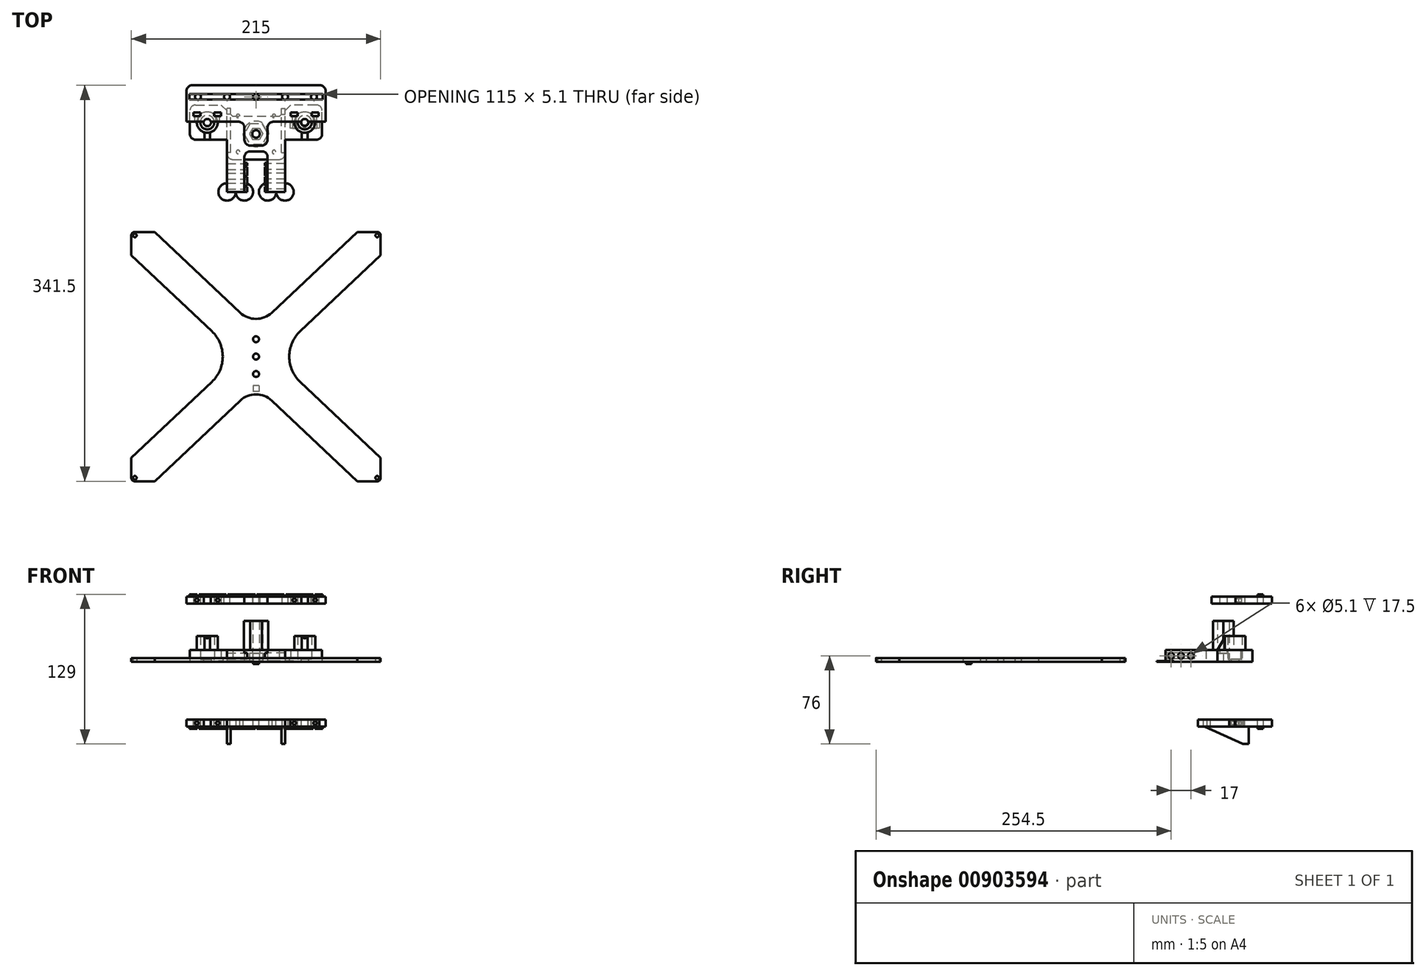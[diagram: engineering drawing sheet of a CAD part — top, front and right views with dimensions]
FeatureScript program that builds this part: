
annotation { "Feature Type Name" : "Feature", "Feature Type Description" : "" }
export const myFeature = defineFeature(function(context is Context, id is Id, definition is map)
    precondition{}
    {
        {
            var Q0;
            Q0=qCreatedBy(makeId("Top.planeOp"),FACE);
            var sketch = newSketch(context, id + "F0", { "sketchPlane" : qUnion([Q0])});
            skArc(sketch, "E0", {"start": v(0, -3.25) * mm, "mid": v(3.25, 0) * mm, "end": v(0, 3.25) * mm});
            skCircle(sketch, "E1", {"center": v(42, 10) * mm, "radius": 3.25 * mm});
            skLineSegment(sketch, "E2", {"start": v(0, -15) * mm, "end": v(5, -15) * mm});
            skLineSegment(sketch, "E3", {"start": v(10, -20) * mm, "end": v(10, -50) * mm});
            skLineSegment(sketch, "E4", {"start": v(10, -50) * mm, "end": v(25, -50) * mm});
            skLineSegment(sketch, "E5", {"start": v(25, -50) * mm, "end": v(25, -5) * mm});
            skLineSegment(sketch, "E6", {"start": v(25, -5) * mm, "end": v(52, -5) * mm});
            skLineSegment(sketch, "E7", {"start": v(57, 0) * mm, "end": v(57, 20) * mm});
            skLineSegment(sketch, "E8", {"start": v(52, 25) * mm, "end": v(30, 25) * mm});
            skLineSegment(sketch, "E9", {"start": v(30, 25) * mm, "end": v(20, 15) * mm});
            skLineSegment(sketch, "E10", {"start": v(20, 15) * mm, "end": v(0, 15) * mm});
            skPoint(sketch, "E11.visualSharp", {"position": v(10, -15) * mm});
            skArc(sketch, "E11.filletArc", {"start": v(10, -20) * mm, "mid": v(8.54, -16.46) * mm, "end": v(5, -15) * mm});
            skLineSegment(sketch, "E12", {"start": v(0, 15) * mm, "end": v(0, 3.25) * mm});
            skCircle(sketch, "E13.cCircle", {"center": v(0, 0) * mm, "radius": 5 * mm, "construction": true});
            skLineSegment(sketch, "E13.0", {"start": v(-2.89, 5) * mm, "end": v(2.89, 5) * mm, "construction": true});
            skLineSegment(sketch, "E13.1", {"start": v(2.89, 5) * mm, "end": v(5.77, 0) * mm, "construction": true});
            skLineSegment(sketch, "E13.2", {"start": v(5.77, 0) * mm, "end": v(2.89, -5) * mm, "construction": true});
            skLineSegment(sketch, "E13.3", {"start": v(2.89, -5) * mm, "end": v(-2.89, -5) * mm, "construction": true});
            skLineSegment(sketch, "E13.4", {"start": v(-2.89, -5) * mm, "end": v(-5.77, 0) * mm, "construction": true});
            skLineSegment(sketch, "E13.5", {"start": v(-5.77, 0) * mm, "end": v(-2.89, 5) * mm, "construction": true});
            skPoint(sketch, "E13.0.midPoint", {"position": v(0, 5) * mm});
            skLineSegment(sketch, "E14.trimOffspring", {"start": v(0, -3.25) * mm, "end": v(0, -15) * mm});
            skPoint(sketch, "E15.visualSharp", {"position": v(57, -5) * mm});
            skArc(sketch, "E15.filletArc", {"start": v(52, -5) * mm, "mid": v(55.54, -3.54) * mm, "end": v(57, 0) * mm});
            skPoint(sketch, "E16.visualSharp", {"position": v(57, 25) * mm});
            skArc(sketch, "E16.filletArc", {"start": v(57, 20) * mm, "mid": v(55.54, 23.54) * mm, "end": v(52, 25) * mm});
            skSolve(sketch);
        }
        {
            var Q0;
            Q0=makeQuery(id+"F0.imprint","IMPRINT",FACE,{"disambiguationData":[TD([[makeQuery(id+"F0.imprint","IMPRINT",EDGE,{"derivedFrom":sQuery(id+"F0.wireOp",EDGE,"E0")}),-1.0]])]});
            extrude(context, id + "F1", {"entities" : qUnion([Q0]), "depth" : 10 * mm});
        }
        {
            var Q0;
            Q0=makeQuery(id+"F1.opExtrude","CAP_FACE",FACE,{"disambiguationData":[OSD([sQuery(id+"F0.wireOp",EDGE,"E0"),sQuery(id+"F0.wireOp",EDGE,"E1"),sQuery(id+"F0.wireOp",EDGE,"E2"),sQuery(id+"F0.wireOp",EDGE,"E3"),sQuery(id+"F0.wireOp",EDGE,"E4"),sQuery(id+"F0.wireOp",EDGE,"E5"),sQuery(id+"F0.wireOp",EDGE,"E6"),sQuery(id+"F0.wireOp",EDGE,"E7"),sQuery(id+"F0.wireOp",EDGE,"E8"),sQuery(id+"F0.wireOp",EDGE,"E9"),sQuery(id+"F0.wireOp",EDGE,"E10"),sQuery(id+"F0.wireOp",EDGE,"E11.filletArc"),sQuery(id+"F0.wireOp",EDGE,"E12"),sQuery(id+"F0.wireOp",EDGE,"E14.trimOffspring"),sQuery(id+"F0.wireOp",EDGE,"E15.filletArc"),sQuery(id+"F0.wireOp",EDGE,"E16.filletArc")])],"isStart":false});
            var sketch = newSketch(context, id + "F2", { "sketchPlane" : qUnion([Q0])});
            skCircle(sketch, "E17", {"center": v(42, 10) * mm, "radius": 6.05 * mm});
            skCircle(sketch, "E18", {"center": v(42, 10) * mm, "radius": 9 * mm});
            skSolve(sketch);
        }
        {
            var Q0;
            Q0=qSketchRegion(id+"F2",true);
            extrude(context, id + "F3", {"entities" : qUnion([Q0]), "operationType" : NewBodyOperationType.ADD, "depth" : 12 * mm});
        }
        {
            var Q0;
            {var subQ0=sQuery(id+"F0.wireOp",EDGE,"E9");var subQ1=sQuery(id+"F0.wireOp",EDGE,"E8");var subQ2=sQuery(id+"F0.wireOp",EDGE,"E16.filletArc");var subQ3=sQuery(id+"F0.wireOp",EDGE,"E7");var subQ4=sQuery(id+"F0.wireOp",EDGE,"E15.filletArc");var subQ5=sQuery(id+"F0.wireOp",EDGE,"E6");var subQ6=sQuery(id+"F0.wireOp",EDGE,"E5");var subQ7=sQuery(id+"F0.wireOp",EDGE,"E0");var subQ8=sQuery(id+"F0.wireOp",EDGE,"E2");var subQ9=sQuery(id+"F0.wireOp",EDGE,"E10");var subQ10=sQuery(id+"F0.wireOp",EDGE,"E3");var subQ11=sQuery(id+"F0.wireOp",EDGE,"E4");var subQ12=sQuery(id+"F0.wireOp",EDGE,"E11.filletArc");var subQ13=sQuery(id+"F0.wireOp",EDGE,"E12");var subQ14=sQuery(id+"F0.wireOp",EDGE,"E14.trimOffspring");Q0=makeQuery(id+"F3.boolean.opBoolean","SPLIT",FACE,{"disambiguationData":[TD([makeQuery(id+"F1.opExtrude","SWEPT_FACE",FACE,{"disambiguationData":[OSD([subQ7])]})])],"derivedFrom":makeQuery(id+"F1.opExtrude","CAP_FACE",FACE,{"disambiguationData":[OSD([subQ7,sQuery(id+"F0.wireOp",EDGE,"E1"),subQ8,subQ10,subQ11,subQ6,subQ5,subQ3,subQ1,subQ0,subQ9,subQ12,subQ13,subQ14,subQ4,subQ2])],"isStart":false})});}
            var sketch = newSketch(context, id + "F4", { "sketchPlane" : qUnion([Q0])});
            skArc(sketch, "E19.cCircle", {"start": v(0, -5) * mm, "mid": v(4.33, -2.5) * mm, "end": v(4.33, 2.5) * mm, "construction": true});
            skLineSegment(sketch, "E19.0", {"start": v(0, 5) * mm, "end": v(2.89, 5) * mm});
            skLineSegment(sketch, "E19.1", {"start": v(2.89, 5) * mm, "end": v(5.77, 0) * mm});
            skLineSegment(sketch, "E19.2", {"start": v(5.77, 0) * mm, "end": v(2.89, -5) * mm});
            skLineSegment(sketch, "E19.3", {"start": v(2.89, -5) * mm, "end": v(0, -5) * mm});
            skPoint(sketch, "E19.0.midPoint", {"position": v(0, 5) * mm});
            skArc(sketch, "E20.cCircle", {"start": v(0, -9) * mm, "mid": v(9, 0) * mm, "end": v(0, 9) * mm, "construction": true});
            skLineSegment(sketch, "E20.0", {"start": v(0, 9) * mm, "end": v(5.2, 9) * mm});
            skLineSegment(sketch, "E20.1", {"start": v(5.2, 9) * mm, "end": v(10.4, 0) * mm});
            skLineSegment(sketch, "E20.2", {"start": v(10.4, 0) * mm, "end": v(5.2, -9) * mm});
            skLineSegment(sketch, "E20.3", {"start": v(5.2, -9) * mm, "end": v(0, -9) * mm});
            skPoint(sketch, "E20.0.midPoint", {"position": v(0, 9) * mm});
            skLineSegment(sketch, "E21", {"start": v(0, 9) * mm, "end": v(0, 5) * mm});
            skLineSegment(sketch, "E22", {"start": v(0, -9.12) * mm, "end": v(0, -5) * mm});
            skSolve(sketch);
        }
        {
            var Q0;
            Q0=qSketchRegion(id+"F4",true);
            extrude(context, id + "F5", {"entities" : qUnion([Q0]), "operationType" : NewBodyOperationType.ADD, "depth" : 25 * mm});
        }
        {
            var Q0;
            {var subQ0=sQuery(id+"F0.wireOp",EDGE,"E11.filletArc");var subQ2=sQuery(id+"F0.wireOp",EDGE,"E9");var subQ4=sQuery(id+"F0.wireOp",EDGE,"E8");var subQ6=sQuery(id+"F0.wireOp",EDGE,"E16.filletArc");var subQ8=sQuery(id+"F0.wireOp",EDGE,"E7");var subQ10=sQuery(id+"F0.wireOp",EDGE,"E15.filletArc");var subQ12=sQuery(id+"F0.wireOp",EDGE,"E6");var subQ14=sQuery(id+"F0.wireOp",EDGE,"E2");var subQ15=makeQuery(id+"F1.opExtrude","SWEPT_FACE",FACE,{"disambiguationData":[OSD([subQ14])]});var subQ16=sQuery(id+"F0.wireOp",EDGE,"E10");var subQ18=sQuery(id+"F0.wireOp",EDGE,"E3");var subQ20=sQuery(id+"F0.wireOp",EDGE,"E4");var subQ22=sQuery(id+"F0.wireOp",EDGE,"E5");var subQ24=sQuery(id+"F0.wireOp",EDGE,"E12");var subQ26=sQuery(id+"F0.wireOp",EDGE,"E14.trimOffspring");var subQ29=sQuery(id+"F0.wireOp",EDGE,"E0");Q0=makeQuery(id+"F5.boolean.opBoolean","SPLIT",FACE,{"disambiguationData":[TD([subQ15])],"derivedFrom":makeQuery(id+"F3.boolean.opBoolean","SPLIT",FACE,{"disambiguationData":[TD([makeQuery(id+"F1.opExtrude","SWEPT_FACE",FACE,{"disambiguationData":[OSD([subQ29])]})])],"derivedFrom":makeQuery(id+"F1.opExtrude","CAP_FACE",FACE,{"disambiguationData":[OSD([subQ29,sQuery(id+"F0.wireOp",EDGE,"E1"),subQ14,subQ18,subQ20,subQ22,subQ12,subQ8,subQ4,subQ2,subQ16,subQ0,subQ24,subQ26,subQ10,subQ6])],"isStart":false})})});}
            var sketch = newSketch(context, id + "F6", { "sketchPlane" : qUnion([Q0])});
            skCircle(sketch, "E23.0", {"center": v(42, 10) * mm, "radius": 6.05 * mm});
            skLineSegment(sketch, "E24.0", {"start": v(0, 5) * mm, "end": v(2.89, 5) * mm});
            skLineSegment(sketch, "E25.0", {"start": v(2.89, 5) * mm, "end": v(5.77, 0) * mm});
            skLineSegment(sketch, "E26.0", {"start": v(5.77, 0) * mm, "end": v(2.89, -5) * mm});
            skLineSegment(sketch, "E27.0", {"start": v(2.89, -5) * mm, "end": v(0, -5) * mm});
            skLineSegment(sketch, "E28", {"start": v(0, 5) * mm, "end": v(0, -5) * mm});
            skSolve(sketch);
        }
        {
            var Q0;
            Q0=makeQuery(id+"F6.imprint","IMPRINT",FACE,{"disambiguationData":[TD([[makeQuery(id+"F6.imprint","IMPRINT",EDGE,{"derivedFrom":sQuery(id+"F6.wireOp",EDGE,"E23.0")}),1.0]])]});
            extrude(context, id + "F7", {"entities" : qUnion([Q0]), "operationType" : NewBodyOperationType.REMOVE, "oppositeDirection" : true, "depth" : 8 * mm});
        }
        {
            var Q0;
            Q0=qCreatedBy(makeId("Right.planeOp"),FACE);
            cPlane(context, id + "F8", {"entities" : qUnion([Q0]), "cplaneType" : CPlaneType.OFFSET, "offset" : 42 * mm, "width" : 150 * mm, "height" : 150 * mm});
        }
        {
            var Q0;
            Q0=makeQuery(id+"F1.opExtrude","CAP_FACE",FACE,{"disambiguationData":[OSD([sQuery(id+"F0.wireOp",EDGE,"E0"),sQuery(id+"F0.wireOp",EDGE,"E1"),sQuery(id+"F0.wireOp",EDGE,"E2"),sQuery(id+"F0.wireOp",EDGE,"E3"),sQuery(id+"F0.wireOp",EDGE,"E4"),sQuery(id+"F0.wireOp",EDGE,"E5"),sQuery(id+"F0.wireOp",EDGE,"E6"),sQuery(id+"F0.wireOp",EDGE,"E7"),sQuery(id+"F0.wireOp",EDGE,"E8"),sQuery(id+"F0.wireOp",EDGE,"E9"),sQuery(id+"F0.wireOp",EDGE,"E10"),sQuery(id+"F0.wireOp",EDGE,"E11.filletArc"),sQuery(id+"F0.wireOp",EDGE,"E12"),sQuery(id+"F0.wireOp",EDGE,"E14.trimOffspring"),sQuery(id+"F0.wireOp",EDGE,"E15.filletArc"),sQuery(id+"F0.wireOp",EDGE,"E16.filletArc")])],"isStart":true});
            var sketch = newSketch(context, id + "F9", { "sketchPlane" : qUnion([Q0])});
            skLineSegment(sketch, "E29.0.0", {"start": v(0, 5) * mm, "end": v(2.89, 5) * mm});
            skLineSegment(sketch, "E29.0.1", {"start": v(2.89, 5) * mm, "end": v(5.77, 0) * mm});
            skLineSegment(sketch, "E29.0.2", {"start": v(5.77, 0) * mm, "end": v(2.89, -5) * mm});
            skLineSegment(sketch, "E29.0.3", {"start": v(2.89, -5) * mm, "end": v(0, -5) * mm});
            skLineSegment(sketch, "E29.0.4", {"start": v(0, -5) * mm, "end": v(0, -3.25) * mm});
            skArc(sketch, "E29.0.5", {"start": v(0, -3.25) * mm, "mid": v(3.25, 0) * mm, "end": v(0, 3.25) * mm});
            skLineSegment(sketch, "E29.0.6", {"start": v(0, 3.25) * mm, "end": v(0, 5) * mm});
            skSolve(sketch);
        }
        {
            var Q0;
            Q0=makeQuery(id+"F9.imprint","IMPRINT",FACE,{"disambiguationData":[TD([[makeQuery(id+"F9.imprint","IMPRINT",EDGE,{"derivedFrom":sQuery(id+"F9.wireOp",EDGE,"E29.0.0")}),-1.0]])]});
            extrude(context, id + "F10", {"entities" : qUnion([Q0]), "operationType" : NewBodyOperationType.REMOVE, "oppositeDirection" : true, "depth" : 7 * mm});
        }
        {
            var Q0;
            Q0=qCreatedBy(id+"F8.planeOp",FACE);
            var sketch = newSketch(context, id + "F11", { "sketchPlane" : qUnion([Q0])});
            skLineSegment(sketch, "E30", {"start": v(2, 22) * mm, "end": v(-4.93, 10) * mm});
            skLineSegment(sketch, "E31", {"start": v(-4.93, 10) * mm, "end": v(2, 10) * mm});
            skLineSegment(sketch, "E32", {"start": v(2, 10) * mm, "end": v(2, 22) * mm});
            skSolve(sketch);
        }
        {
            var Q0;
            Q0=makeQuery(id+"F11.imprint","IMPRINT",FACE,{"disambiguationData":[TD([[makeQuery(id+"F11.imprint","IMPRINT",EDGE,{"derivedFrom":sQuery(id+"F11.wireOp",EDGE,"E30")}),1.0]])]});
            extrude(context, id + "F12", {"entities" : qUnion([Q0]), "operationType" : NewBodyOperationType.ADD, "endBound" : BoundingType.SYMMETRIC, "depth" : 5 * mm});
        }
        {
            var Q0;
            Q0=makeQuery(id+"F1.opExtrude","SWEPT_FACE",FACE,{"disambiguationData":[OSD([sQuery(id+"F0.wireOp",EDGE,"E4")])]});
            var sketch = newSketch(context, id + "F13", { "sketchPlane" : qUnion([Q0])});
            skLineSegment(sketch, "E33.bottom", {"start": v(10, 7.5) * mm, "end": v(7.5, 7.5) * mm});
            skLineSegment(sketch, "E33.top", {"start": v(10, 2.5) * mm, "end": v(7.5, 2.5) * mm});
            skLineSegment(sketch, "E33.left", {"start": v(10, 7.5) * mm, "end": v(10, 2.5) * mm});
            skLineSegment(sketch, "E33.right", {"start": v(7.5, 7.5) * mm, "end": v(7.5, 2.5) * mm});
            skSolve(sketch);
        }
        {
            var Q0;
            Q0=qSketchRegion(id+"F13",true);
            extrude(context, id + "F14", {"entities" : qUnion([Q0]), "operationType" : NewBodyOperationType.ADD, "oppositeDirection" : true, "depth" : 25 * mm});
        }
        {
            var Q0;
            Q0=makeQuery(id+"F14.opExtrude","SWEPT_FACE",FACE,{"disambiguationData":[OSD([sQuery(id+"F13.wireOp",EDGE,"E33.right")])]});
            var sketch = newSketch(context, id + "F15", { "sketchPlane" : qUnion([Q0])});
            skCircle(sketch, "E34", {"center": v(45, 5) * mm, "radius": 2.55 * mm});
            skPoint(sketch, "E34.centerSnap0", {"position": v(50, 5) * mm});
            skCircle(sketch, "E35.1.0.0", {"center": v(36.5, 5) * mm, "radius": 2.55 * mm});
            skCircle(sketch, "E35.2.0.0", {"center": v(28, 5) * mm, "radius": 2.55 * mm});
            skLineSegment(sketch, "E35.direction1", {"start": v(45, 5) * mm, "end": v(36.5, 5) * mm, "construction": true});
            skSolve(sketch);
        }
        {
            var Q0;
            Q0=qSketchRegion(id+"F15",true);
            extrude(context, id + "F16", {"entities" : qUnion([Q0]), "operationType" : NewBodyOperationType.REMOVE, "oppositeDirection" : true, "depth" : 25 * mm});
        }
        {
            var Q0;
            Q0=makeQuery(id+"F1.opExtrude","SWEPT_BODY",BODY,{"disambiguationData":[OSD([sQuery(id+"F0.wireOp",EDGE,"E0"),sQuery(id+"F0.wireOp",EDGE,"E1"),sQuery(id+"F0.wireOp",EDGE,"E2"),sQuery(id+"F0.wireOp",EDGE,"E3"),sQuery(id+"F0.wireOp",EDGE,"E4"),sQuery(id+"F0.wireOp",EDGE,"E5"),sQuery(id+"F0.wireOp",EDGE,"E6"),sQuery(id+"F0.wireOp",EDGE,"E7"),sQuery(id+"F0.wireOp",EDGE,"E8"),sQuery(id+"F0.wireOp",EDGE,"E9"),sQuery(id+"F0.wireOp",EDGE,"E10"),sQuery(id+"F0.wireOp",EDGE,"E11.filletArc"),sQuery(id+"F0.wireOp",EDGE,"E12"),sQuery(id+"F0.wireOp",EDGE,"E14.trimOffspring"),sQuery(id+"F0.wireOp",EDGE,"E15.filletArc"),sQuery(id+"F0.wireOp",EDGE,"E16.filletArc")])]});
            var Q1;
            Q1=qCreatedBy(makeId("Right.planeOp"),FACE);
            mirror(context, id + "F17", {"operationType" : NewBodyOperationType.ADD, "entities" : qUnion([Q0]), "mirrorPlane" : qUnion([Q1])});
        }
        {
            var Q0;
            Q0=qCreatedBy(makeId("Top.planeOp"),FACE);
            cPlane(context, id + "F18", {"entities" : qUnion([Q0]), "cplaneType" : CPlaneType.OFFSET, "offset" : 50 * mm, "width" : 150 * mm, "height" : 150 * mm});
        }
        {
            var Q0;
            Q0=qCreatedBy(id+"F18.planeOp",FACE);
            var sketch = newSketch(context, id + "F19", { "sketchPlane" : qUnion([Q0])});
            skArc(sketch, "E36.0", {"start": v(-39.04, 10.5) * mm, "mid": v(-42, 13) * mm, "end": v(-44.96, 10.5) * mm});
            skCircle(sketch, "E37.0", {"center": v(0, 0) * mm, "radius": 3.25 * mm});
            skArc(sketch, "E38.0", {"start": v(44.96, 10.5) * mm, "mid": v(42, 13) * mm, "end": v(39.04, 10.5) * mm});
            skLineSegment(sketch, "E39", {"start": v(-60, 10.5) * mm, "end": v(-60, 37) * mm});
            skLineSegment(sketch, "E40", {"start": v(-55, 42) * mm, "end": v(55, 42) * mm});
            skLineSegment(sketch, "E41", {"start": v(60, 37) * mm, "end": v(60, 10.5) * mm});
            skArc(sketch, "E42.filletArc", {"start": v(-55, 42) * mm, "mid": v(-58.54, 40.54) * mm, "end": v(-60, 37) * mm});
            skPoint(sketch, "E43.visualSharp", {"position": v(60, 42) * mm});
            skArc(sketch, "E43.filletArc", {"start": v(60, 37) * mm, "mid": v(58.54, 40.54) * mm, "end": v(55, 42) * mm});
            skLineSegment(sketch, "E44", {"start": v(-10, 5.5) * mm, "end": v(-10, -5) * mm});
            skLineSegment(sketch, "E45", {"start": v(-5, -10) * mm, "end": v(5, -10) * mm});
            skLineSegment(sketch, "E46", {"start": v(10, -5) * mm, "end": v(10, 5.5) * mm});
            skLineSegment(sketch, "E47", {"start": v(15, 10.5) * mm, "end": v(39.04, 10.5) * mm});
            skLineSegment(sketch, "E48", {"start": v(-15, 10.5) * mm, "end": v(-39.04, 10.5) * mm});
            skLineSegment(sketch, "E49", {"start": v(0, 0) * mm, "end": v(0, -10) * mm, "construction": true});
            skLineSegment(sketch, "E50", {"start": v(60, 10.5) * mm, "end": v(44.96, 10.5) * mm});
            skLineSegment(sketch, "E51", {"start": v(-60, 10.5) * mm, "end": v(-44.96, 10.5) * mm});
            skLineSegment(sketch, "E52.bottom", {"start": v(-54, 18.5) * mm, "end": v(-48, 18.5) * mm});
            skLineSegment(sketch, "E52.top", {"start": v(-54, 15.5) * mm, "end": v(-48, 15.5) * mm});
            skLineSegment(sketch, "E52.left", {"start": v(-54, 18.5) * mm, "end": v(-54, 15.5) * mm});
            skLineSegment(sketch, "E52.right", {"start": v(-48, 18.5) * mm, "end": v(-48, 15.5) * mm});
            skLineSegment(sketch, "E53", {"start": v(-42, 10) * mm, "end": v(-42, 18.5) * mm, "construction": true});
            skLineSegment(sketch, "E54", {"start": v(-51, 18.5) * mm, "end": v(-51, 15.5) * mm, "construction": true});
            skLineSegment(sketch, "E55.MirrorCS", {"start": v(-36, 18.5) * mm, "end": v(-36, 15.5) * mm});
            skLineSegment(sketch, "E56.MirrorCS", {"start": v(-30, 18.5) * mm, "end": v(-36, 18.5) * mm});
            skLineSegment(sketch, "E57.MirrorCS", {"start": v(-30, 18.5) * mm, "end": v(-30, 15.5) * mm});
            skLineSegment(sketch, "E58.MirrorCS", {"start": v(-30, 15.5) * mm, "end": v(-36, 15.5) * mm});
            skLineSegment(sketch, "E59.MirrorCS", {"start": v(30, 15.5) * mm, "end": v(36, 15.5) * mm});
            skLineSegment(sketch, "E60.MirrorCS", {"start": v(30, 18.5) * mm, "end": v(36, 18.5) * mm});
            skLineSegment(sketch, "E61.MirrorCS", {"start": v(30, 18.5) * mm, "end": v(30, 15.5) * mm});
            skLineSegment(sketch, "E62.MirrorCS", {"start": v(36, 18.5) * mm, "end": v(36, 15.5) * mm});
            skLineSegment(sketch, "E63.MirrorCS", {"start": v(48, 18.5) * mm, "end": v(48, 15.5) * mm});
            skLineSegment(sketch, "E64.MirrorCS", {"start": v(54, 18.5) * mm, "end": v(48, 18.5) * mm});
            skLineSegment(sketch, "E65.MirrorCS", {"start": v(54, 18.5) * mm, "end": v(54, 15.5) * mm});
            skLineSegment(sketch, "E66.MirrorCS", {"start": v(54, 15.5) * mm, "end": v(48, 15.5) * mm});
            skPoint(sketch, "E67.visualSharp", {"position": v(-10, 10.5) * mm});
            skArc(sketch, "E67.filletArc", {"start": v(-10, 5.5) * mm, "mid": v(-11.46, 9.04) * mm, "end": v(-15, 10.5) * mm});
            skPoint(sketch, "E68.visualSharp", {"position": v(10, 10.5) * mm});
            skArc(sketch, "E68.filletArc", {"start": v(15, 10.5) * mm, "mid": v(11.46, 9.04) * mm, "end": v(10, 5.5) * mm});
            skPoint(sketch, "E69.visualSharp", {"position": v(10, -10) * mm});
            skArc(sketch, "E69.filletArc", {"start": v(5, -10) * mm, "mid": v(8.54, -8.54) * mm, "end": v(10, -5) * mm});
            skPoint(sketch, "E70.visualSharp", {"position": v(-10, -10) * mm});
            skArc(sketch, "E70.filletArc", {"start": v(-10, -5) * mm, "mid": v(-8.54, -8.54) * mm, "end": v(-5, -10) * mm});
            skSolve(sketch);
        }
        {
            var Q0;
            Q0=makeQuery(id+"F19.imprint","IMPRINT",FACE,{"disambiguationData":[TD([[makeQuery(id+"F19.imprint","IMPRINT",EDGE,{"derivedFrom":sQuery(id+"F19.wireOp",EDGE,"E36.0")}),-1.0]])]});
            extrude(context, id + "F20", {"entities" : qUnion([Q0]), "depth" : 6 * mm});
        }
        {
            var Q0;
            Q0=makeQuery(id+"F20.opExtrude","SWEPT_FACE",FACE,{"disambiguationData":[OSD([sQuery(id+"F19.wireOp",EDGE,"E52.top")])]});
            var sketch = newSketch(context, id + "F21", { "sketchPlane" : qUnion([Q0])});
            skCircle(sketch, "E71", {"center": v(51, 53) * mm, "radius": 1.55 * mm});
            skPoint(sketch, "E71.centerSnap0", {"position": v(51, 56) * mm});
            skLineSegment(sketch, "E72", {"start": v(54, 53) * mm, "end": v(51, 53) * mm, "construction": true});
            skCircle(sketch, "E73", {"center": v(33, 53) * mm, "radius": 1.55 * mm});
            skLineSegment(sketch, "E74", {"start": v(0, 59.79) * mm, "end": v(0, 45.57) * mm, "construction": true});
            skCircle(sketch, "E75.MirrorC", {"center": v(-33, 53) * mm, "radius": 1.55 * mm});
            skCircle(sketch, "E76.MirrorC", {"center": v(-51, 53) * mm, "radius": 1.55 * mm});
            skSolve(sketch);
        }
        {
            var Q0;
            Q0=qSketchRegion(id+"F21",true);
            extrude(context, id + "F22", {"entities" : qUnion([Q0]), "operationType" : NewBodyOperationType.REMOVE, "oppositeDirection" : true, "depth" : 10 * mm});
        }
        {
            var Q0;
            Q0=qCreatedBy(makeId("Right.planeOp"),FACE);
            var sketch = newSketch(context, id + "F23", { "sketchPlane" : qUnion([Q0])});
            skLineSegment(sketch, "E77", {"start": v(29.55, 56) * mm, "end": v(29.55, 58) * mm});
            skLineSegment(sketch, "E78", {"start": v(29.55, 58) * mm, "end": v(34.45, 58) * mm});
            skLineSegment(sketch, "E79", {"start": v(34.45, 58) * mm, "end": v(34.45, 56) * mm});
            skPoint(sketch, "E80", {"position": v(32, 58) * mm});
            skLineSegment(sketch, "E81", {"start": v(29.55, 56) * mm, "end": v(34.45, 56) * mm});
            skSolve(sketch);
        }
        {
            var Q0;
            Q0=makeQuery(id+"F23.imprint","IMPRINT",FACE,{"disambiguationData":[TD([[makeQuery(id+"F23.imprint","IMPRINT",EDGE,{"derivedFrom":sQuery(id+"F23.wireOp",EDGE,"E77")}),-1.0]])]});
            extrude(context, id + "F24", {"entities" : qUnion([Q0]), "operationType" : NewBodyOperationType.ADD, "endBound" : BoundingType.SYMMETRIC, "depth" : 115 * mm});
        }
        {
            var Q0;
            Q0=makeQuery(id+"F24.opExtrude","SWEPT_FACE",FACE,{"disambiguationData":[OSD([sQuery(id+"F23.wireOp",EDGE,"E78")])]});
            var sketch = newSketch(context, id + "F25", { "sketchPlane" : qUnion([Q0])});
            skCircle(sketch, "E82", {"center": v(0, 32) * mm, "radius": 2.55 * mm});
            skCircle(sketch, "E83", {"center": v(25, 32) * mm, "radius": 2.55 * mm});
            skCircle(sketch, "E84", {"center": v(50, 32) * mm, "radius": 2.55 * mm});
            skCircle(sketch, "E85", {"center": v(-25, 32) * mm, "radius": 2.55 * mm});
            skCircle(sketch, "E86", {"center": v(-50, 32) * mm, "radius": 2.55 * mm});
            skLineSegment(sketch, "E87", {"start": v(-50, 32) * mm, "end": v(-25, 32) * mm, "construction": true});
            skLineSegment(sketch, "E88", {"start": v(-25, 32) * mm, "end": v(0, 32) * mm, "construction": true});
            skLineSegment(sketch, "E89", {"start": v(25, 32) * mm, "end": v(0, 32) * mm, "construction": true});
            skLineSegment(sketch, "E90", {"start": v(50, 32) * mm, "end": v(25, 32) * mm, "construction": true});
            skSolve(sketch);
        }
        {
            var Q0;
            Q0=qSketchRegion(id+"F25",true);
            extrude(context, id + "F26", {"entities" : qUnion([Q0]), "operationType" : NewBodyOperationType.REMOVE, "oppositeDirection" : true, "depth" : 10 * mm});
        }
        {
            var Q0;
            Q0=qCreatedBy(makeId("Top.planeOp"),FACE);
            cPlane(context, id + "F27", {"entities" : qUnion([Q0]), "cplaneType" : CPlaneType.OFFSET, "offset" : 50 * mm, "oppositeDirection" : true, "width" : 150 * mm, "height" : 150 * mm});
        }
        {
            var Q0;
            Q0=qCreatedBy(id+"F27.planeOp",FACE);
            var sketch = newSketch(context, id + "F28", { "sketchPlane" : qUnion([Q0])});
            skArc(sketch, "E91.0", {"start": v(-39.04, 10.5) * mm, "mid": v(-42, 13) * mm, "end": v(-44.96, 10.5) * mm});
            skLineSegment(sketch, "E92.0", {"start": v(-60, 10.5) * mm, "end": v(-44.96, 10.5) * mm});
            skArc(sketch, "E93.0", {"start": v(44.96, 10.5) * mm, "mid": v(42, 13) * mm, "end": v(39.04, 10.5) * mm});
            skLineSegment(sketch, "E94.0", {"start": v(60, 10.5) * mm, "end": v(44.96, 10.5) * mm});
            skLineSegment(sketch, "E95.0", {"start": v(60, 37) * mm, "end": v(60, 10.5) * mm});
            skArc(sketch, "E96.0", {"start": v(60, 37) * mm, "mid": v(58.54, 40.54) * mm, "end": v(55, 42) * mm});
            skLineSegment(sketch, "E97.0", {"start": v(-55, 42) * mm, "end": v(55, 42) * mm});
            skArc(sketch, "E98.0", {"start": v(-55, 42) * mm, "mid": v(-58.54, 40.54) * mm, "end": v(-60, 37) * mm});
            skLineSegment(sketch, "E99.0", {"start": v(-60, 10.5) * mm, "end": v(-60, 37) * mm});
            skLineSegment(sketch, "E100.0", {"start": v(-54, 18.5) * mm, "end": v(-48, 18.5) * mm});
            skLineSegment(sketch, "E101.0", {"start": v(-48, 18.5) * mm, "end": v(-48, 15.5) * mm});
            skLineSegment(sketch, "E102.0", {"start": v(-54, 15.5) * mm, "end": v(-48, 15.5) * mm});
            skLineSegment(sketch, "E103.0", {"start": v(-54, 18.5) * mm, "end": v(-54, 15.5) * mm});
            skLineSegment(sketch, "E104.0", {"start": v(-30, 18.5) * mm, "end": v(-36, 18.5) * mm});
            skLineSegment(sketch, "E105.0", {"start": v(-36, 18.5) * mm, "end": v(-36, 15.5) * mm});
            skLineSegment(sketch, "E106.0", {"start": v(-30, 15.5) * mm, "end": v(-36, 15.5) * mm});
            skLineSegment(sketch, "E107.0", {"start": v(-30, 18.5) * mm, "end": v(-30, 15.5) * mm});
            skLineSegment(sketch, "E108.0", {"start": v(30, 18.5) * mm, "end": v(30, 15.5) * mm});
            skLineSegment(sketch, "E109.0", {"start": v(30, 18.5) * mm, "end": v(36, 18.5) * mm});
            skLineSegment(sketch, "E110.0", {"start": v(36, 18.5) * mm, "end": v(36, 15.5) * mm});
            skLineSegment(sketch, "E111.0", {"start": v(30, 15.5) * mm, "end": v(36, 15.5) * mm});
            skLineSegment(sketch, "E112.0", {"start": v(48, 18.5) * mm, "end": v(48, 15.5) * mm});
            skLineSegment(sketch, "E113.0", {"start": v(54, 18.5) * mm, "end": v(48, 18.5) * mm});
            skLineSegment(sketch, "E114.0", {"start": v(54, 18.5) * mm, "end": v(54, 15.5) * mm});
            skLineSegment(sketch, "E115.0", {"start": v(54, 15.5) * mm, "end": v(48, 15.5) * mm});
            skCircle(sketch, "E116", {"center": v(0, 0) * mm, "radius": 11 * mm});
            skLineSegment(sketch, "E117.bottom", {"start": v(-15.5, -15.5) * mm, "end": v(15.5, -15.5) * mm, "construction": true});
            skLineSegment(sketch, "E117.top", {"start": v(-15.5, 15.5) * mm, "end": v(15.5, 15.5) * mm, "construction": true});
            skLineSegment(sketch, "E117.left", {"start": v(-15.5, -15.5) * mm, "end": v(-15.5, 15.5) * mm, "construction": true});
            skLineSegment(sketch, "E117.right", {"start": v(15.5, -15.5) * mm, "end": v(15.5, 15.5) * mm, "construction": true});
            skCircle(sketch, "E118", {"center": v(-15.5, -15.5) * mm, "radius": 1.55 * mm});
            skCircle(sketch, "E119", {"center": v(15.5, -15.5) * mm, "radius": 1.55 * mm});
            skCircle(sketch, "E120", {"center": v(15.5, 15.5) * mm, "radius": 1.55 * mm});
            skCircle(sketch, "E121", {"center": v(-15.5, 15.5) * mm, "radius": 1.55 * mm});
            skLineSegment(sketch, "E122", {"start": v(-20, -22) * mm, "end": v(20, -22) * mm});
            skPoint(sketch, "E123", {"position": v(0, -22) * mm});
            skLineSegment(sketch, "E124", {"start": v(-25, -17) * mm, "end": v(-25, 8) * mm});
            skLineSegment(sketch, "E125", {"start": v(25, -17) * mm, "end": v(25, 8) * mm});
            skLineSegment(sketch, "E126.trimOffspring", {"start": v(-27.5, 10.5) * mm, "end": v(-39.04, 10.5) * mm});
            skLineSegment(sketch, "E127.trimOffspring", {"start": v(27.5, 10.5) * mm, "end": v(39.04, 10.5) * mm});
            skPoint(sketch, "E128.visualSharp", {"position": v(-25, -22) * mm});
            skArc(sketch, "E128.filletArc", {"start": v(-25, -17) * mm, "mid": v(-23.54, -20.54) * mm, "end": v(-20, -22) * mm});
            skPoint(sketch, "E129.visualSharp", {"position": v(-25, 10.5) * mm});
            skArc(sketch, "E129.filletArc", {"start": v(-25, 8) * mm, "mid": v(-25.73, 9.77) * mm, "end": v(-27.5, 10.5) * mm});
            skPoint(sketch, "E130.visualSharp", {"position": v(25, -22) * mm});
            skArc(sketch, "E130.filletArc", {"start": v(20, -22) * mm, "mid": v(23.54, -20.54) * mm, "end": v(25, -17) * mm});
            skPoint(sketch, "E131.visualSharp", {"position": v(25, 10.5) * mm});
            skArc(sketch, "E131.filletArc", {"start": v(27.5, 10.5) * mm, "mid": v(25.73, 9.77) * mm, "end": v(25, 8) * mm});
            skSolve(sketch);
        }
        {
            var Q0;
            Q0=makeQuery(id+"F28.imprint","IMPRINT",FACE,{"disambiguationData":[TD([[makeQuery(id+"F28.imprint","IMPRINT",EDGE,{"derivedFrom":sQuery(id+"F28.wireOp",EDGE,"E91.0")}),-1.0]])]});
            extrude(context, id + "F29", {"entities" : qUnion([Q0]), "oppositeDirection" : true, "depth" : 6 * mm});
        }
        {
            var Q0;
            Q0=makeQuery(id+"F29.opExtrude","SWEPT_FACE",FACE,{"disambiguationData":[OSD([sQuery(id+"F28.wireOp",EDGE,"E102.0")])]});
            var sketch = newSketch(context, id + "F30", { "sketchPlane" : qUnion([Q0])});
            skCircle(sketch, "E132", {"center": v(51, -53) * mm, "radius": 1.55 * mm});
            skPoint(sketch, "E132.centerSnap0", {"position": v(54, -53) * mm});
            skPoint(sketch, "E132.centerSnap1", {"position": v(51, -50) * mm});
            skCircle(sketch, "E133", {"center": v(33, -53) * mm, "radius": 1.55 * mm});
            skLineSegment(sketch, "E134", {"start": v(0, -41.03) * mm, "end": v(0, -69.82) * mm, "construction": true});
            skCircle(sketch, "E135.MirrorC", {"center": v(-33, -53) * mm, "radius": 1.55 * mm});
            skCircle(sketch, "E136.MirrorC", {"center": v(-51, -53) * mm, "radius": 1.55 * mm});
            skSolve(sketch);
        }
        {
            var Q0;
            Q0=qSketchRegion(id+"F30",true);
            extrude(context, id + "F31", {"entities" : qUnion([Q0]), "operationType" : NewBodyOperationType.REMOVE, "oppositeDirection" : true, "depth" : 10 * mm});
        }
        {
            var Q0;
            Q0=qCreatedBy(makeId("Right.planeOp"),FACE);
            var sketch = newSketch(context, id + "F32", { "sketchPlane" : qUnion([Q0])});
            skLineSegment(sketch, "E137", {"start": v(34.45, -56) * mm, "end": v(34.45, -58) * mm});
            skLineSegment(sketch, "E138", {"start": v(34.45, -58) * mm, "end": v(29.55, -58) * mm});
            skLineSegment(sketch, "E139", {"start": v(29.55, -58) * mm, "end": v(29.55, -56) * mm});
            skLineSegment(sketch, "E140", {"start": v(29.55, -56) * mm, "end": v(34.45, -56) * mm});
            skPoint(sketch, "E141", {"position": v(32, -58) * mm});
            skSolve(sketch);
        }
        {
            var Q0;
            Q0=makeQuery(id+"F32.imprint","IMPRINT",FACE,{"disambiguationData":[TD([[makeQuery(id+"F32.imprint","IMPRINT",EDGE,{"derivedFrom":sQuery(id+"F32.wireOp",EDGE,"E137")}),-1.0]])]});
            extrude(context, id + "F33", {"entities" : qUnion([Q0]), "operationType" : NewBodyOperationType.ADD, "endBound" : BoundingType.SYMMETRIC, "depth" : 115 * mm});
        }
        {
            var Q0;
            Q0=makeQuery(id+"F29.opExtrude","CAP_FACE",FACE,{"disambiguationData":[OSD([sQuery(id+"F28.wireOp",EDGE,"E91.0"),sQuery(id+"F28.wireOp",EDGE,"E92.0"),sQuery(id+"F28.wireOp",EDGE,"E93.0"),sQuery(id+"F28.wireOp",EDGE,"E94.0"),sQuery(id+"F28.wireOp",EDGE,"E95.0"),sQuery(id+"F28.wireOp",EDGE,"E96.0"),sQuery(id+"F28.wireOp",EDGE,"E97.0"),sQuery(id+"F28.wireOp",EDGE,"E98.0"),sQuery(id+"F28.wireOp",EDGE,"E99.0"),sQuery(id+"F28.wireOp",EDGE,"E100.0"),sQuery(id+"F28.wireOp",EDGE,"E101.0"),sQuery(id+"F28.wireOp",EDGE,"E102.0"),sQuery(id+"F28.wireOp",EDGE,"E103.0"),sQuery(id+"F28.wireOp",EDGE,"E104.0"),sQuery(id+"F28.wireOp",EDGE,"E105.0"),sQuery(id+"F28.wireOp",EDGE,"E106.0"),sQuery(id+"F28.wireOp",EDGE,"E107.0"),sQuery(id+"F28.wireOp",EDGE,"E108.0"),sQuery(id+"F28.wireOp",EDGE,"E109.0"),sQuery(id+"F28.wireOp",EDGE,"E110.0"),sQuery(id+"F28.wireOp",EDGE,"E111.0"),sQuery(id+"F28.wireOp",EDGE,"E112.0"),sQuery(id+"F28.wireOp",EDGE,"E113.0"),sQuery(id+"F28.wireOp",EDGE,"E114.0"),sQuery(id+"F28.wireOp",EDGE,"E115.0"),sQuery(id+"F28.wireOp",EDGE,"E116"),sQuery(id+"F28.wireOp",EDGE,"E118"),sQuery(id+"F28.wireOp",EDGE,"E119"),sQuery(id+"F28.wireOp",EDGE,"E120"),sQuery(id+"F28.wireOp",EDGE,"E121"),sQuery(id+"F28.wireOp",EDGE,"E122"),sQuery(id+"F28.wireOp",EDGE,"E124"),sQuery(id+"F28.wireOp",EDGE,"E125"),sQuery(id+"F28.wireOp",EDGE,"E126.trimOffspring"),sQuery(id+"F28.wireOp",EDGE,"E127.trimOffspring"),sQuery(id+"F28.wireOp",EDGE,"E128.filletArc"),sQuery(id+"F28.wireOp",EDGE,"E129.filletArc"),sQuery(id+"F28.wireOp",EDGE,"E130.filletArc"),sQuery(id+"F28.wireOp",EDGE,"E131.filletArc")])],"isStart":true});
            var sketch = newSketch(context, id + "F34", { "sketchPlane" : qUnion([Q0])});
            skCircle(sketch, "E142.0", {"center": v(-50, 32) * mm, "radius": 2.55 * mm});
            skCircle(sketch, "E143.0", {"center": v(-25, 32) * mm, "radius": 2.55 * mm});
            skCircle(sketch, "E144.0", {"center": v(0, 32) * mm, "radius": 2.55 * mm});
            skCircle(sketch, "E145.0", {"center": v(25, 32) * mm, "radius": 2.55 * mm});
            skCircle(sketch, "E146.0", {"center": v(50, 32) * mm, "radius": 2.55 * mm});
            skSolve(sketch);
        }
        {
            var Q0;
            Q0=qSketchRegion(id+"F34",true);
            extrude(context, id + "F35", {"entities" : qUnion([Q0]), "operationType" : NewBodyOperationType.REMOVE, "oppositeDirection" : true, "depth" : 10 * mm});
        }
        {
            var Q0;
            Q0=makeQuery(id+"F29.opExtrude","SWEPT_FACE",FACE,{"disambiguationData":[OSD([sQuery(id+"F28.wireOp",EDGE,"E125")])]});
            var sketch = newSketch(context, id + "F36", { "sketchPlane" : qUnion([Q0])});
            skLineSegment(sketch, "E147", {"start": v(-16.1, -56) * mm, "end": v(16.9, -71) * mm});
            skLineSegment(sketch, "E148", {"start": v(16.9, -71) * mm, "end": v(21.9, -71) * mm});
            skLineSegment(sketch, "E149", {"start": v(21.9, -71) * mm, "end": v(21.9, -56) * mm});
            skLineSegment(sketch, "E150", {"start": v(-16.1, -56) * mm, "end": v(21.9, -56) * mm});
            skSolve(sketch);
        }
        {
            var Q0;
            Q0=qSketchRegion(id+"F36",true);
            extrude(context, id + "F37", {"entities" : qUnion([Q0]), "operationType" : NewBodyOperationType.ADD, "oppositeDirection" : true, "depth" : 3 * mm});
        }
        {
            var Q0;
            Q0=makeQuery(id+"F29.opExtrude","SWEPT_BODY",BODY,{"disambiguationData":[OSD([sQuery(id+"F28.wireOp",EDGE,"E91.0"),sQuery(id+"F28.wireOp",EDGE,"E92.0"),sQuery(id+"F28.wireOp",EDGE,"E93.0"),sQuery(id+"F28.wireOp",EDGE,"E94.0"),sQuery(id+"F28.wireOp",EDGE,"E95.0"),sQuery(id+"F28.wireOp",EDGE,"E96.0"),sQuery(id+"F28.wireOp",EDGE,"E97.0"),sQuery(id+"F28.wireOp",EDGE,"E98.0"),sQuery(id+"F28.wireOp",EDGE,"E99.0"),sQuery(id+"F28.wireOp",EDGE,"E100.0"),sQuery(id+"F28.wireOp",EDGE,"E101.0"),sQuery(id+"F28.wireOp",EDGE,"E102.0"),sQuery(id+"F28.wireOp",EDGE,"E103.0"),sQuery(id+"F28.wireOp",EDGE,"E104.0"),sQuery(id+"F28.wireOp",EDGE,"E105.0"),sQuery(id+"F28.wireOp",EDGE,"E106.0"),sQuery(id+"F28.wireOp",EDGE,"E107.0"),sQuery(id+"F28.wireOp",EDGE,"E108.0"),sQuery(id+"F28.wireOp",EDGE,"E109.0"),sQuery(id+"F28.wireOp",EDGE,"E110.0"),sQuery(id+"F28.wireOp",EDGE,"E111.0"),sQuery(id+"F28.wireOp",EDGE,"E112.0"),sQuery(id+"F28.wireOp",EDGE,"E113.0"),sQuery(id+"F28.wireOp",EDGE,"E114.0"),sQuery(id+"F28.wireOp",EDGE,"E115.0"),sQuery(id+"F28.wireOp",EDGE,"E116"),sQuery(id+"F28.wireOp",EDGE,"E118"),sQuery(id+"F28.wireOp",EDGE,"E119"),sQuery(id+"F28.wireOp",EDGE,"E120"),sQuery(id+"F28.wireOp",EDGE,"E121"),sQuery(id+"F28.wireOp",EDGE,"E122"),sQuery(id+"F28.wireOp",EDGE,"E124"),sQuery(id+"F28.wireOp",EDGE,"E125"),sQuery(id+"F28.wireOp",EDGE,"E126.trimOffspring"),sQuery(id+"F28.wireOp",EDGE,"E127.trimOffspring"),sQuery(id+"F28.wireOp",EDGE,"E128.filletArc"),sQuery(id+"F28.wireOp",EDGE,"E129.filletArc"),sQuery(id+"F28.wireOp",EDGE,"E130.filletArc"),sQuery(id+"F28.wireOp",EDGE,"E131.filletArc")])]});
            var Q1;
            Q1=qCreatedBy(makeId("Right.planeOp"),FACE);
            mirror(context, id + "F38", {"operationType" : NewBodyOperationType.ADD, "entities" : qUnion([Q0]), "mirrorPlane" : qUnion([Q1])});
        }
        {
            var Q0;
            Q0=makeQuery(id+"F29.opExtrude","CAP_FACE",FACE,{"disambiguationData":[OSD([sQuery(id+"F28.wireOp",EDGE,"E91.0"),sQuery(id+"F28.wireOp",EDGE,"E92.0"),sQuery(id+"F28.wireOp",EDGE,"E93.0"),sQuery(id+"F28.wireOp",EDGE,"E94.0"),sQuery(id+"F28.wireOp",EDGE,"E95.0"),sQuery(id+"F28.wireOp",EDGE,"E96.0"),sQuery(id+"F28.wireOp",EDGE,"E97.0"),sQuery(id+"F28.wireOp",EDGE,"E98.0"),sQuery(id+"F28.wireOp",EDGE,"E99.0"),sQuery(id+"F28.wireOp",EDGE,"E100.0"),sQuery(id+"F28.wireOp",EDGE,"E101.0"),sQuery(id+"F28.wireOp",EDGE,"E102.0"),sQuery(id+"F28.wireOp",EDGE,"E103.0"),sQuery(id+"F28.wireOp",EDGE,"E104.0"),sQuery(id+"F28.wireOp",EDGE,"E105.0"),sQuery(id+"F28.wireOp",EDGE,"E106.0"),sQuery(id+"F28.wireOp",EDGE,"E107.0"),sQuery(id+"F28.wireOp",EDGE,"E108.0"),sQuery(id+"F28.wireOp",EDGE,"E109.0"),sQuery(id+"F28.wireOp",EDGE,"E110.0"),sQuery(id+"F28.wireOp",EDGE,"E111.0"),sQuery(id+"F28.wireOp",EDGE,"E112.0"),sQuery(id+"F28.wireOp",EDGE,"E113.0"),sQuery(id+"F28.wireOp",EDGE,"E114.0"),sQuery(id+"F28.wireOp",EDGE,"E115.0"),sQuery(id+"F28.wireOp",EDGE,"E116"),sQuery(id+"F28.wireOp",EDGE,"E118"),sQuery(id+"F28.wireOp",EDGE,"E119"),sQuery(id+"F28.wireOp",EDGE,"E120"),sQuery(id+"F28.wireOp",EDGE,"E121"),sQuery(id+"F28.wireOp",EDGE,"E122"),sQuery(id+"F28.wireOp",EDGE,"E124"),sQuery(id+"F28.wireOp",EDGE,"E125"),sQuery(id+"F28.wireOp",EDGE,"E126.trimOffspring"),sQuery(id+"F28.wireOp",EDGE,"E127.trimOffspring"),sQuery(id+"F28.wireOp",EDGE,"E128.filletArc"),sQuery(id+"F28.wireOp",EDGE,"E129.filletArc"),sQuery(id+"F28.wireOp",EDGE,"E130.filletArc"),sQuery(id+"F28.wireOp",EDGE,"E131.filletArc")])],"isStart":true});
            var sketch = newSketch(context, id + "F39", { "sketchPlane" : qUnion([Q0])});
            skArc(sketch, "E151", {"start": v(39, 10) * mm, "mid": v(42, 7) * mm, "end": v(45, 10) * mm});
            skLineSegment(sketch, "E152", {"start": v(45, 10) * mm, "end": v(54.5, 10) * mm});
            skLineSegment(sketch, "E153", {"start": v(54.5, 10) * mm, "end": v(54.5, 5) * mm});
            skLineSegment(sketch, "E154", {"start": v(54.5, 5) * mm, "end": v(29.5, 5) * mm});
            skLineSegment(sketch, "E155", {"start": v(29.5, 5) * mm, "end": v(29.5, 10) * mm});
            skLineSegment(sketch, "E156", {"start": v(29.5, 10) * mm, "end": v(39, 10) * mm});
            skSolve(sketch);
        }
        {
            var Q0;
            Q0=qSketchRegion(id+"F39",true);
            extrude(context, id + "F40", {"entities" : qUnion([Q0]), "oppositeDirection" : true, "depth" : 6 * mm});
        }
        {
            var Q0;
            Q0=makeQuery(id+"F40.opExtrude","SWEPT_FACE",FACE,{"disambiguationData":[OSD([sQuery(id+"F39.wireOp",EDGE,"E154")])]});
            var sketch = newSketch(context, id + "F41", { "sketchPlane" : qUnion([Q0])});
            skCircle(sketch, "E157.0", {"center": v(33, -53) * mm, "radius": 1.55 * mm});
            skCircle(sketch, "E158.0", {"center": v(51, -53) * mm, "radius": 1.55 * mm});
            skSolve(sketch);
        }
        {
            var Q0;
            Q0=qSketchRegion(id+"F41",true);
            extrude(context, id + "F42", {"entities" : qUnion([Q0]), "operationType" : NewBodyOperationType.REMOVE, "oppositeDirection" : true, "depth" : 6 * mm});
        }
        {
            var Q0;
            Q0=qCreatedBy(makeId("Top.planeOp"),FACE);
            var sketch = newSketch(context, id + "F43", { "sketchPlane" : qUnion([Q0])});
            skLineSegment(sketch, "E159.bottom", {"start": v(104.5, -87.5) * mm, "end": v(-104.5, -87.5) * mm, "construction": true});
            skLineSegment(sketch, "E159.top", {"start": v(104.5, -296.5) * mm, "end": v(-104.5, -296.5) * mm, "construction": true});
            skLineSegment(sketch, "E159.left", {"start": v(104.5, -87.5) * mm, "end": v(104.5, -296.5) * mm, "construction": true});
            skLineSegment(sketch, "E159.right", {"start": v(-104.5, -87.5) * mm, "end": v(-104.5, -296.5) * mm, "construction": true});
            skPoint(sketch, "E159.middle", {"position": v(0, -192) * mm});
            skCircle(sketch, "E160", {"center": v(-104.5, -87.5) * mm, "radius": 1.55 * mm});
            skCircle(sketch, "E161", {"center": v(104.5, -87.5) * mm, "radius": 1.55 * mm});
            skCircle(sketch, "E162", {"center": v(104.5, -296.5) * mm, "radius": 1.55 * mm});
            skCircle(sketch, "E163", {"center": v(-104.5, -296.5) * mm, "radius": 1.55 * mm});
            skLineSegment(sketch, "E164.bottom", {"start": v(15, -167) * mm, "end": v(-15, -167) * mm, "construction": true});
            skLineSegment(sketch, "E164.top", {"start": v(15, -217) * mm, "end": v(-15, -217) * mm, "construction": true});
            skLineSegment(sketch, "E164.left", {"start": v(15, -167) * mm, "end": v(15, -217) * mm, "construction": true});
            skLineSegment(sketch, "E164.right", {"start": v(-15, -167) * mm, "end": v(-15, -217) * mm, "construction": true});
            skLineSegment(sketch, "E165", {"start": v(87.36, -84.5) * mm, "end": v(104.5, -84.5) * mm});
            skLineSegment(sketch, "E166", {"start": v(107.5, -87.5) * mm, "end": v(107.5, -104.65) * mm});
            skPoint(sketch, "E167.visualSharp", {"position": v(107.5, -84.5) * mm});
            skArc(sketch, "E167.filletArc", {"start": v(107.5, -87.5) * mm, "mid": v(106.62, -85.38) * mm, "end": v(104.5, -84.5) * mm});
            skLineSegment(sketch, "E168", {"start": v(87.36, -84.5) * mm, "end": v(13.73, -154.03) * mm});
            skLineSegment(sketch, "E169", {"start": v(107.5, -104.65) * mm, "end": v(38.1, -170.2) * mm});
            skLineSegment(sketch, "E170", {"start": v(87.36, -299.5) * mm, "end": v(104.5, -299.5) * mm});
            skLineSegment(sketch, "E171", {"start": v(107.5, -296.5) * mm, "end": v(107.5, -279.36) * mm});
            skPoint(sketch, "E172.visualSharp", {"position": v(107.5, -299.5) * mm});
            skArc(sketch, "E172.filletArc", {"start": v(104.5, -299.5) * mm, "mid": v(106.62, -298.62) * mm, "end": v(107.5, -296.5) * mm});
            skLineSegment(sketch, "E173", {"start": v(107.5, -279.36) * mm, "end": v(38.1, -213.81) * mm});
            skLineSegment(sketch, "E174", {"start": v(87.36, -299.5) * mm, "end": v(13.73, -229.97) * mm});
            skLineSegment(sketch, "E175", {"start": v(0, -192) * mm, "end": v(0, -167) * mm, "construction": true});
            skLineSegment(sketch, "E176.MirrorCS", {"start": v(-87.36, -84.5) * mm, "end": v(-13.73, -154.03) * mm});
            skLineSegment(sketch, "E177.MirrorCS", {"start": v(-107.5, -104.65) * mm, "end": v(-38.1, -170.2) * mm});
            skLineSegment(sketch, "E178.MirrorCS", {"start": v(-107.5, -279.36) * mm, "end": v(-38.1, -213.81) * mm});
            skLineSegment(sketch, "E179.MirrorCS", {"start": v(-87.36, -299.5) * mm, "end": v(-13.73, -229.97) * mm});
            skLineSegment(sketch, "E180.MirrorCS", {"start": v(-87.36, -299.5) * mm, "end": v(-104.5, -299.5) * mm});
            skArc(sketch, "E181.MirrorCS", {"start": v(-104.5, -299.5) * mm, "mid": v(-106.62, -298.62) * mm, "end": v(-107.5, -296.5) * mm});
            skLineSegment(sketch, "E182.MirrorCS", {"start": v(-107.5, -296.5) * mm, "end": v(-107.5, -279.36) * mm});
            skLineSegment(sketch, "E183.MirrorCS", {"start": v(-87.36, -84.5) * mm, "end": v(-104.5, -84.5) * mm});
            skLineSegment(sketch, "E184.MirrorCS", {"start": v(-107.5, -87.5) * mm, "end": v(-107.5, -104.65) * mm});
            skArc(sketch, "E185.MirrorCS", {"start": v(-107.5, -87.5) * mm, "mid": v(-106.62, -85.38) * mm, "end": v(-104.5, -84.5) * mm});
            skArc(sketch, "E186", {"start": v(-38.1, -213.81) * mm, "mid": v(-28.7, -192) * mm, "end": v(-38.1, -170.2) * mm});
            skArc(sketch, "E187", {"start": v(-13.73, -154.03) * mm, "mid": v(0, -159.5) * mm, "end": v(13.73, -154.03) * mm});
            skArc(sketch, "E188", {"start": v(38.1, -170.2) * mm, "mid": v(28.7, -192) * mm, "end": v(38.1, -213.81) * mm});
            skArc(sketch, "E189", {"start": v(13.73, -229.97) * mm, "mid": v(0, -224.51) * mm, "end": v(-13.73, -229.97) * mm});
            skPoint(sketch, "E190.orphan", {"position": v(-15, -192) * mm});
            skPoint(sketch, "E191.orphan", {"position": v(0, -167) * mm});
            skPoint(sketch, "E192.orphan", {"position": v(15, -192) * mm});
            skPoint(sketch, "E193.orphan", {"position": v(0, -217) * mm});
            skCircle(sketch, "E194", {"center": v(0, -192) * mm, "radius": 2.55 * mm});
            skCircle(sketch, "E195", {"center": v(0, -177) * mm, "radius": 2.55 * mm});
            skCircle(sketch, "E196", {"center": v(0, -207) * mm, "radius": 2.55 * mm});
            skSolve(sketch);
        }
        {
            var Q0;
            Q0=qSketchRegion(id+"F43",true);
            extrude(context, id + "F44", {"entities" : qUnion([Q0]), "depth" : 3.17 * mm});
        }
        {
            var Q0;
            Q0=makeQuery(id+"F44.opExtrude","CAP_FACE",FACE,{"disambiguationData":[OSD([sQuery(id+"F43.wireOp",EDGE,"E160"),sQuery(id+"F43.wireOp",EDGE,"E161"),sQuery(id+"F43.wireOp",EDGE,"E162"),sQuery(id+"F43.wireOp",EDGE,"E163"),sQuery(id+"F43.wireOp",EDGE,"E165"),sQuery(id+"F43.wireOp",EDGE,"E166"),sQuery(id+"F43.wireOp",EDGE,"E167.filletArc"),sQuery(id+"F43.wireOp",EDGE,"E168"),sQuery(id+"F43.wireOp",EDGE,"E169"),sQuery(id+"F43.wireOp",EDGE,"E170"),sQuery(id+"F43.wireOp",EDGE,"E171"),sQuery(id+"F43.wireOp",EDGE,"E172.filletArc"),sQuery(id+"F43.wireOp",EDGE,"E173"),sQuery(id+"F43.wireOp",EDGE,"E174"),sQuery(id+"F43.wireOp",EDGE,"E176.MirrorCS"),sQuery(id+"F43.wireOp",EDGE,"E177.MirrorCS"),sQuery(id+"F43.wireOp",EDGE,"E178.MirrorCS"),sQuery(id+"F43.wireOp",EDGE,"E179.MirrorCS"),sQuery(id+"F43.wireOp",EDGE,"E180.MirrorCS"),sQuery(id+"F43.wireOp",EDGE,"E181.MirrorCS"),sQuery(id+"F43.wireOp",EDGE,"E182.MirrorCS"),sQuery(id+"F43.wireOp",EDGE,"E183.MirrorCS"),sQuery(id+"F43.wireOp",EDGE,"E184.MirrorCS"),sQuery(id+"F43.wireOp",EDGE,"E185.MirrorCS"),sQuery(id+"F43.wireOp",EDGE,"E186"),sQuery(id+"F43.wireOp",EDGE,"E187"),sQuery(id+"F43.wireOp",EDGE,"E188"),sQuery(id+"F43.wireOp",EDGE,"E189"),sQuery(id+"F43.wireOp",EDGE,"E194"),sQuery(id+"F43.wireOp",EDGE,"E195"),sQuery(id+"F43.wireOp",EDGE,"E196")])],"isStart":true});
            var sketch = newSketch(context, id + "F45", { "sketchPlane" : qUnion([Q0])});
            skLineSegment(sketch, "E197.bottom", {"start": v(2.5, 217.05) * mm, "end": v(-2.5, 217.05) * mm});
            skLineSegment(sketch, "E197.top", {"start": v(2.5, 222.05) * mm, "end": v(-2.5, 222.05) * mm});
            skLineSegment(sketch, "E197.left", {"start": v(2.5, 217.05) * mm, "end": v(2.5, 222.05) * mm});
            skLineSegment(sketch, "E197.right", {"start": v(-2.5, 217.05) * mm, "end": v(-2.5, 222.05) * mm});
            skPoint(sketch, "E197.middle", {"position": v(0, 219.55) * mm});
            skSolve(sketch);
        }
        {
            var Q0;
            Q0=qSketchRegion(id+"F45",true);
            extrude(context, id + "F46", {"entities" : qUnion([Q0]), "operationType" : NewBodyOperationType.ADD, "depth" : 2 * mm});
        }
        {
            var Q0;
            {var subQ0=makeQuery(id+"F1.opExtrude","CAP_FACE",FACE,{"disambiguationData":[OSD([sQuery(id+"F0.wireOp",EDGE,"E0"),sQuery(id+"F0.wireOp",EDGE,"E1"),sQuery(id+"F0.wireOp",EDGE,"E2"),sQuery(id+"F0.wireOp",EDGE,"E3"),sQuery(id+"F0.wireOp",EDGE,"E4"),sQuery(id+"F0.wireOp",EDGE,"E5"),sQuery(id+"F0.wireOp",EDGE,"E6"),sQuery(id+"F0.wireOp",EDGE,"E7"),sQuery(id+"F0.wireOp",EDGE,"E8"),sQuery(id+"F0.wireOp",EDGE,"E9"),sQuery(id+"F0.wireOp",EDGE,"E10"),sQuery(id+"F0.wireOp",EDGE,"E11.filletArc"),sQuery(id+"F0.wireOp",EDGE,"E12"),sQuery(id+"F0.wireOp",EDGE,"E14.trimOffspring"),sQuery(id+"F0.wireOp",EDGE,"E15.filletArc"),sQuery(id+"F0.wireOp",EDGE,"E16.filletArc")])],"isStart":true});Q0=makeQuery(id+"F17.boolean.opBoolean","MERGE",FACE,{"derivedFrom":[subQ0,makeQuery(id+"F17.opPattern","COPY",FACE,{"derivedFrom":subQ0,"instanceName":"1"})]});}
            var sketch = newSketch(context, id + "F47", { "sketchPlane" : qUnion([Q0])});
            skArc(sketch, "E198", {"start": v(25, 42.5) * mm, "mid": v(30.3, 55.3) * mm, "end": v(17.5, 50) * mm});
            skArc(sketch, "E199", {"start": v(17.5, 50) * mm, "mid": v(4.7, 55.3) * mm, "end": v(10, 42.5) * mm});
            skArc(sketch, "E200", {"start": v(-10, 42.5) * mm, "mid": v(-4.7, 55.3) * mm, "end": v(-17.5, 50) * mm});
            skArc(sketch, "E201", {"start": v(-17.5, 50) * mm, "mid": v(-30.3, 55.3) * mm, "end": v(-25, 42.5) * mm});
            skLineSegment(sketch, "E202.0.8", {"start": v(25, 42.5) * mm, "end": v(25, 50) * mm});
            skLineSegment(sketch, "E202.0.9", {"start": v(25, 50) * mm, "end": v(10, 50) * mm});
            skLineSegment(sketch, "E202.0.14", {"start": v(-10, 42.5) * mm, "end": v(-10, 50) * mm});
            skLineSegment(sketch, "E202.0.15", {"start": v(-10, 50) * mm, "end": v(-25, 50) * mm});
            skLineSegment(sketch, "E202.0.16", {"start": v(-25, 50) * mm, "end": v(-25, 42.5) * mm});
            skLineSegment(sketch, "E203", {"start": v(10, 50) * mm, "end": v(10, 42.5) * mm});
            skSolve(sketch);
        }
        {
            var Q0;
            Q0=qSketchRegion(id+"F47",true);
            extrude(context, id + "F48", {"entities" : qUnion([Q0]), "operationType" : NewBodyOperationType.ADD, "oppositeDirection" : true, "depth" : .5 * mm, "offsetDistance" : 25 * mm});
        }
    });
